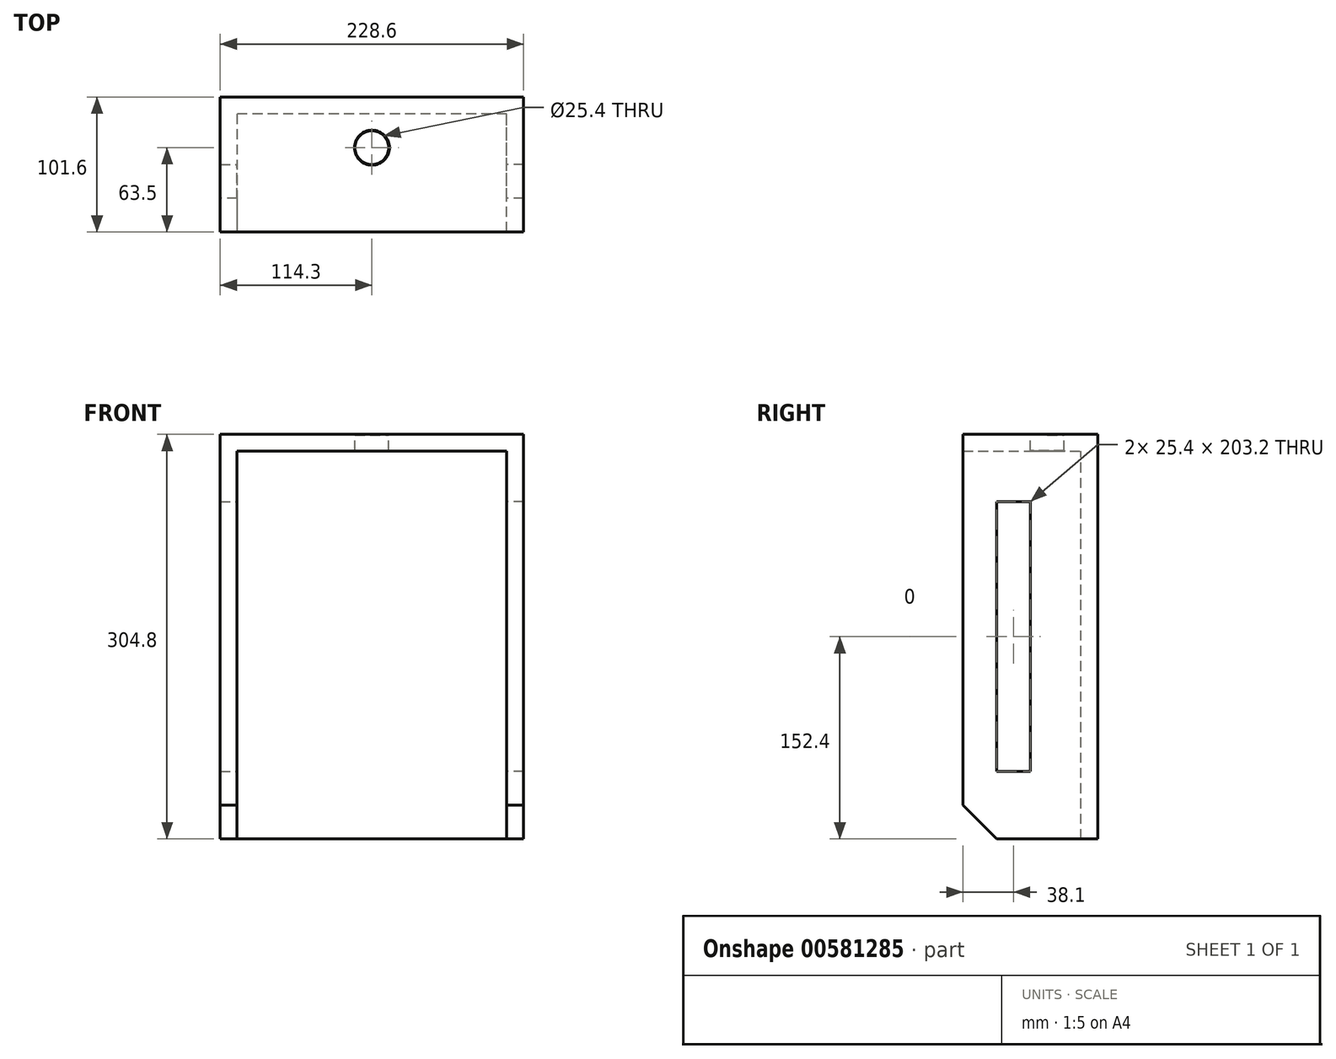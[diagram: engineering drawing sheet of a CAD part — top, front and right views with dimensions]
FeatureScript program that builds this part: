
annotation { "Feature Type Name" : "Feature", "Feature Type Description" : "" }
export const myFeature = defineFeature(function(context is Context, id is Id, definition is map)
    precondition{}
    {
        {
            var Q0;
            Q0=qCreatedBy(makeId("Front.planeOp"),FACE);
            var sketch = newSketch(context, id + "F0", { "sketchPlane" : qUnion([Q0])});
            skLineSegment(sketch, "E0.bottom", {"start": v(101.6, -152.4) * mm, "end": v(-101.6, -152.4) * mm});
            skLineSegment(sketch, "E0.top", {"start": v(101.6, 152.4) * mm, "end": v(-101.6, 152.4) * mm});
            skLineSegment(sketch, "E0.left", {"start": v(101.6, -152.4) * mm, "end": v(101.6, 152.4) * mm});
            skLineSegment(sketch, "E0.right", {"start": v(-101.6, -152.4) * mm, "end": v(-101.6, 152.4) * mm});
            skPoint(sketch, "E0.middle", {"position": v(0, 0) * mm});
            skSolve(sketch);
        }
        {
            var Q0;
            Q0=makeQuery(id+"F0.imprint","IMPRINT",FACE,{"disambiguationData":[TD([[makeQuery(id+"F0.imprint","IMPRINT",EDGE,{"derivedFrom":sQuery(id+"F0.wireOp",EDGE,"E0.bottom")}),-1.0]])]});
            extrude(context, id + "F1", {"entities" : qUnion([Q0]), "endBound" : BoundingType.SYMMETRIC, "depth" : 12.7 * mm, "offsetDistance" : 25.4 * mm});
        }
        {
            var Q0;
            Q0=makeQuery(id+"F1.opExtrude","SWEPT_FACE",FACE,{"disambiguationData":[OSD([sQuery(id+"F0.wireOp",EDGE,"E0.left")])]});
            var sketch = newSketch(context, id + "F2", { "sketchPlane" : qUnion([Q0])});
            skLineSegment(sketch, "E1.bottom", {"start": v(6.35, -152.4) * mm, "end": v(-95.25, -152.4) * mm});
            skLineSegment(sketch, "E1.top", {"start": v(6.35, 152.4) * mm, "end": v(-95.25, 152.4) * mm});
            skLineSegment(sketch, "E1.left", {"start": v(6.35, -152.4) * mm, "end": v(6.35, 152.4) * mm});
            skLineSegment(sketch, "E1.right", {"start": v(-95.25, -152.4) * mm, "end": v(-95.25, 152.4) * mm});
            skLineSegment(sketch, "E2.bottom", {"start": v(-69.85, -101.6) * mm, "end": v(-44.45, -101.6) * mm});
            skLineSegment(sketch, "E2.top", {"start": v(-69.85, 101.6) * mm, "end": v(-44.45, 101.6) * mm});
            skLineSegment(sketch, "E2.left", {"start": v(-69.85, -101.6) * mm, "end": v(-69.85, 101.6) * mm});
            skLineSegment(sketch, "E2.right", {"start": v(-44.45, -101.6) * mm, "end": v(-44.45, 101.6) * mm});
            skPoint(sketch, "E2.middle", {"position": v(-57.15, 0) * mm});
            skPoint(sketch, "E2.middle.positionSnap0", {"position": v(-6.35, 0) * mm});
            skPoint(sketch, "E2.centerSnap0", {"position": v(-6.35, 0) * mm});
            skSolve(sketch);
        }
        {
            var Q0;
            {var subQ0=sQuery(id+"F2.wireOp",EDGE,"E1.left");Q0=makeQuery(id+"F2.imprint","IMPRINT",FACE,{"disambiguationData":[TD([[makeQuery(id+"F2.imprint","IMPRINT",EDGE,{"derivedFrom":subQ0}),1.0]])]});}
            var Q1;
            {var subQ2=sQuery(id+"F2.wireOp",EDGE,"E1.right");Q1=makeQuery(id+"F2.imprint","IMPRINT",FACE,{"disambiguationData":[TD([[makeQuery(id+"F2.imprint","IMPRINT",EDGE,{"derivedFrom":subQ2}),-1.0]])]});}
            extrude(context, id + "F3", {"entities" : qUnion([Q0, Q1]), "operationType" : NewBodyOperationType.ADD, "depth" : 12.7 * mm, "offsetDistance" : 25.4 * mm});
        }
        {
            var Q0;
            Q0=makeQuery(id+"F1.opExtrude","SWEPT_FACE",FACE,{"disambiguationData":[OSD([sQuery(id+"F0.wireOp",EDGE,"E0.right")])]});
            var sketch = newSketch(context, id + "F4", { "sketchPlane" : qUnion([Q0])});
            skLineSegment(sketch, "E3.bottom", {"start": v(-6.35, 152.4) * mm, "end": v(95.25, 152.4) * mm});
            skLineSegment(sketch, "E3.top", {"start": v(-6.35, -152.4) * mm, "end": v(95.25, -152.4) * mm});
            skLineSegment(sketch, "E3.left", {"start": v(-6.35, 152.4) * mm, "end": v(-6.35, -152.4) * mm});
            skLineSegment(sketch, "E3.right", {"start": v(95.25, 152.4) * mm, "end": v(95.25, -152.4) * mm});
            skLineSegment(sketch, "E4.bottom", {"start": v(69.85, -101.6) * mm, "end": v(44.45, -101.6) * mm});
            skLineSegment(sketch, "E4.top", {"start": v(69.85, 101.6) * mm, "end": v(44.45, 101.6) * mm});
            skLineSegment(sketch, "E4.left", {"start": v(69.85, -101.6) * mm, "end": v(69.85, 101.6) * mm});
            skLineSegment(sketch, "E4.right", {"start": v(44.45, -101.6) * mm, "end": v(44.45, 101.6) * mm});
            skPoint(sketch, "E4.middle", {"position": v(57.15, 0) * mm});
            skSolve(sketch);
        }
        {
            var Q0;
            {var subQ2=sQuery(id+"F4.wireOp",EDGE,"E3.right");Q0=makeQuery(id+"F4.imprint","IMPRINT",FACE,{"disambiguationData":[TD([[makeQuery(id+"F4.imprint","IMPRINT",EDGE,{"derivedFrom":subQ2}),-1.0]])]});}
            var Q1;
            {var subQ0=sQuery(id+"F4.wireOp",EDGE,"E3.left");Q1=makeQuery(id+"F4.imprint","IMPRINT",FACE,{"disambiguationData":[TD([[makeQuery(id+"F4.imprint","IMPRINT",EDGE,{"derivedFrom":subQ0}),-1.0]])]});}
            extrude(context, id + "F5", {"entities" : qUnion([Q0, Q1]), "operationType" : NewBodyOperationType.ADD, "depth" : 12.7 * mm, "offsetDistance" : 25.4 * mm});
        }
        {
            var Q0;
            Q0=makeQuery(id+"F5.boolean.opBoolean","MERGE",FACE,{"derivedFrom":[makeQuery(id+"F3.boolean.opBoolean","MERGE",FACE,{"derivedFrom":[makeQuery(id+"F1.opExtrude","SWEPT_FACE",FACE,{"disambiguationData":[OSD([sQuery(id+"F0.wireOp",EDGE,"E0.top")])]}),makeQuery(id+"F3.opExtrude","SWEPT_FACE",FACE,{"disambiguationData":[OSD([sQuery(id+"F2.wireOp",EDGE,"E1.top")])]})]}),makeQuery(id+"F5.opExtrude","SWEPT_FACE",FACE,{"disambiguationData":[OSD([sQuery(id+"F4.wireOp",EDGE,"E3.bottom")])]})]});
            var sketch = newSketch(context, id + "F6", { "sketchPlane" : qUnion([Q0])});
            skLineSegment(sketch, "E5.bottom", {"start": v(-114.3, -95.25) * mm, "end": v(114.3, -95.25) * mm});
            skLineSegment(sketch, "E5.top", {"start": v(-114.3, 6.35) * mm, "end": v(114.3, 6.35) * mm});
            skLineSegment(sketch, "E5.left", {"start": v(-114.3, -95.25) * mm, "end": v(-114.3, 6.35) * mm});
            skLineSegment(sketch, "E5.right", {"start": v(114.3, -95.25) * mm, "end": v(114.3, 6.35) * mm});
            skCircle(sketch, "E6", {"center": v(0, -31.75) * mm, "radius": 12.7 * mm});
            skSolve(sketch);
        }
        {
            var Q0;
            Q0=makeQuery(id+"F6.imprint","IMPRINT",FACE,{"disambiguationData":[TD([[makeQuery(id+"F6.imprint","IMPRINT",EDGE,{"derivedFrom":sQuery(id+"F6.wireOp",EDGE,"E6")}),-1.0]])]});
            extrude(context, id + "F7", {"entities" : qUnion([Q0]), "operationType" : NewBodyOperationType.ADD, "oppositeDirection" : true, "depth" : 12.7 * mm, "offsetDistance" : 25.4 * mm});
        }
        {
            var Q0;
            Q0=makeQuery(id+"F7.opExtrude","CAP_EDGE",EDGE,{"disambiguationData":[OSD([sQuery(id+"F6.wireOp",EDGE,"E6")])],"isStart":true});
            var Q1;
            Q1=makeQuery(id+"F7.opExtrude","CAP_EDGE",EDGE,{"disambiguationData":[OSD([sQuery(id+"F6.wireOp",EDGE,"E6")])],"isStart":false});
            chamfer(context, id + "F8", {"entities" : qUnion([Q0, Q1]), "width" : 0.5 * mm, "tangentPropagation" : true});
        }
        {
            var Q0;
            Q0=makeQuery(id+"F3.opExtrude","SWEPT_EDGE",EDGE,{"disambiguationData":[OSD([sQuery(id+"F2.wireOp",EDGE,"E1.bottom"),sQuery(id+"F2.wireOp",EDGE,"E1.right")])]});
            var Q1;
            Q1=makeQuery(id+"F5.opExtrude","SWEPT_EDGE",EDGE,{"disambiguationData":[OSD([sQuery(id+"F4.wireOp",EDGE,"E3.top"),sQuery(id+"F4.wireOp",EDGE,"E3.right")])]});
            chamfer(context, id + "F9", {"entities" : qUnion([Q0, Q1]), "width" : 25.4 * mm, "tangentPropagation" : true});
        }
    });
